# Revit family: Casement_36_I_Top_Hung_Standard
name_source: partatom
category: Windows
revit_build: Autodesk Revit 2014 (Build: 20130308_1515(x64)
units: mm (PartAtom-declared; Revit-internal decimal feet)

## types (24) — shared parameters
Aluminium Thickness = 1 mm  [stored 0.00328084 ft]
Bead SG Gap = 13 mm  [stored 0.0426509 ft]
Bottom Hung = No
Casement Dimension = 36 mm  [stored 0.11811 ft]
Custom Sash Bottom Height = 554 mm  [stored 1.81759 ft]
Custom Sash Top Height = 554 mm  [stored 1.81759 ft]
DG Extrusion Start = 8 mm  [stored 0.0262467 ft]
DG Gasket Finish = Double Glazing Gasket Material
Default Sill Height = 800 mm  [stored 2.62467 ft]
Depth Bead = 22 mm  [stored 0.0721785 ft]
Description = Window 36mm, Type I top hung
Frame Center Offset = 18 mm  [stored 0.0590551 ft]
Height Panel 1 = 540 mm  [stored 1.77165 ft]
Height Panel 2 = 540 mm  [stored 1.77165 ft]
Height Sash Bottom = 524 mm  [stored 1.71916 ft]
Height Sash Bottom Opening = 554 mm  [stored 1.81759 ft]
Height Sash Top = 524 mm  [stored 1.71916 ft]
Height Sash Top Opening = 554 mm  [stored 1.81759 ft]
Limit Fixed Pane Height Max = 1800 mm
Limit Fixed Pane Height Min = 200 mm  [stored 0.656168 ft]
Limit Fixed Pane Width Max = 1500 mm
Limit Fixed Pane Width Min = 200 mm  [stored 0.656168 ft]
Limit Sash Bottom Height Min = 300 mm  [stored 0.984252 ft]
Limit Sash Top Height Max = 900 mm  [stored 2.95276 ft]
Limit Sash Top Height Min = 300 mm  [stored 0.984252 ft]
Limit Sash Width Max = 1200 mm
Limit Sash Width Min = 300 mm  [stored 0.984252 ft]
Limit Window Height Max = 1860 mm
Limit Window Height Min = 1400 mm
Manufacturer = Crealco
Max System DG One Piece Thickness = 6 mm  [stored 0.019685 ft]
Max System DG Unit Thickness = 25 mm  [stored 0.082021 ft]
Model = Casement 36
Offset Bead SG Center Reversed = 18 mm  [stored 0.0590551 ft]
Offset Panel 3 Bead Top = 1170 mm
Offset Sash 1 Top = 23 mm  [stored 0.0754593 ft]
Offset Sash 2 Top = 593 mm  [stored 1.94554 ft]
Offset Sash Left = 23 mm  [stored 0.0754593 ft]
Offset Transom 1 Top = 570 mm  [stored 1.87008 ft]
Offset Transom 2 Top = 1140 mm
Offset Window Exterior = 18 mm  [stored 0.0590551 ft]
SG Gasket Thickness = 6 mm  [stored 0.019685 ft]
Sash Center Offset = 15 mm  [stored 0.0492126 ft]
Sash Overlap = 7 mm  [stored 0.0229659 ft]
Sash Spacing Inner = 8 mm  [stored 0.0262467 ft]
Top Hung = Yes
URL = http://www.crealco.co.za
Wall Closure = By host
Width Bead = 15 mm  [stored 0.0492126 ft]
Width Profile = 30 mm  [stored 0.0984252 ft]
zero-valued in all types: Window Exterior Offset

## per-type parameters (varying)
- 36-1215DT-1000Pa: Area Pane Left Bottom=0.15 m²; Area Pane Left Middle=0.23 m²; Area Pane Left Top=0.23 m²; Area Pane Right=0.78 m²; Clearvue Insulated LowE SHGC Value=0.695; Clearvue Insulated LowE U Value=5.21; Clearvue Insulated SHGC Value=0.762; Clearvue Insulated U Value=5.93; Clearvue SHGC Value=0.866; Clearvue U Value=8.94; Custom Sash Width=554 mm  [stored 1.81759 ft]; Custom Windload=1000 mm; Custom Window Height=1490 mm; Custom Window Width=1190 mm; DG Thickness Calc=4 mm  [stored 0.0131234 ft]; Depth Mullion=54 mm  [stored 0.177165 ft]; Energy Advantage SHGC Value=0.776; Energy Advantage U Value=6.89; Height=1490 mm; Height Panel 3=290 mm  [stored 0.951444 ft]; Height Panel 4=1430 mm; Intruderprufe Insulated LowE SHGC Value=0.641; Intruderprufe Insulated LowE U Value=5.09; Intruderprufe Insulated SHGC Value=0.699; Intruderprufe Insulated U Value=5.78; Intruderprufe LowE SHGC Value=0.727; Intruderprufe LowE U Value=6.73; Intruderprufe SHGC Value=0.825; Intruderprufe U Value=8.74; Length Mullion=1490 mm; Length Transom=540 mm  [stored 1.77165 ft]; Limit Sash Bottom Height Max=644 mm  [stored 2.11286 ft]; Limit Sash Bottom Height Max Based On Top Sash=644 mm  [stored 2.11286 ft]; Limit Sash Bottom Height Max Calc=644 mm  [stored 2.11286 ft]; Limit Window Width Max=2130 mm; Limit Window Width Min=830 mm  [stored 2.7231 ft]; Max Pane Area=0.78 m²; Mullion Depth Windload Based=54 mm  [stored 0.177165 ft]; Offset Mullion Left=570 mm  [stored 1.87008 ft]; Offset Panel 4 Left=600 mm  [stored 1.9685 ft]; Width=1190 mm; Width Panel 1=540 mm  [stored 1.77165 ft]; Width Panel 2=540 mm  [stored 1.77165 ft]; Width Panel 3=540 mm  [stored 1.77165 ft]; Width Panel 4=560 mm  [stored 1.83727 ft]; Width Sash 1=524 mm  [stored 1.71916 ft]; Width Sash 2=524 mm  [stored 1.71916 ft]; Width Sash Opening=554 mm  [stored 1.81759 ft]; Windload Design=1000 mm
- 36-1515DT-1000Pa: Area Pane Left Bottom=0.15 m²; Area Pane Left Middle=0.23 m²; Area Pane Left Top=0.23 m²; Area Pane Right=1.21 m²; Clearvue Insulated LowE SHGC Value=0.809; Clearvue Insulated LowE U Value=5.28; Clearvue Insulated SHGC Value=0.888; Clearvue Insulated U Value=6.15; Clearvue SHGC Value=1.009; Clearvue U Value=9.7; Custom Sash Width=554 mm  [stored 1.81759 ft]; Custom Windload=1000 mm; Custom Window Height=1490 mm; Custom Window Width=1490 mm; DG Thickness Calc=4 mm  [stored 0.0131234 ft]; Depth Mullion=54 mm  [stored 0.177165 ft]; Energy Advantage SHGC Value=0.903; Energy Advantage U Value=7.27; Height=1490 mm; Height Panel 3=290 mm  [stored 0.951444 ft]; Height Panel 4=1430 mm; Intruderprufe Insulated LowE SHGC Value=0.745; Intruderprufe Insulated LowE U Value=5.16; Intruderprufe Insulated SHGC Value=0.815; Intruderprufe Insulated U Value=6; Intruderprufe LowE SHGC Value=0.845; Intruderprufe LowE U Value=7.1; Intruderprufe SHGC Value=0.96; Intruderprufe U Value=9.48; Length Mullion=1490 mm; Length Transom=540 mm  [stored 1.77165 ft]; Limit Sash Bottom Height Max=644 mm  [stored 2.11286 ft]; Limit Sash Bottom Height Max Based On Top Sash=644 mm  [stored 2.11286 ft]; Limit Sash Bottom Height Max Calc=644 mm  [stored 2.11286 ft]; Limit Window Width Max=2130 mm; Limit Window Width Min=830 mm  [stored 2.7231 ft]; Max Pane Area=1.21 m²; Mullion Depth Windload Based=54 mm  [stored 0.177165 ft]; Offset Mullion Left=570 mm  [stored 1.87008 ft]; Offset Panel 4 Left=600 mm  [stored 1.9685 ft]; Width=1490 mm; Width Panel 1=540 mm  [stored 1.77165 ft]; Width Panel 2=540 mm  [stored 1.77165 ft]; Width Panel 3=540 mm  [stored 1.77165 ft]; Width Panel 4=860 mm  [stored 2.82152 ft]; Width Sash 1=524 mm  [stored 1.71916 ft]; Width Sash 2=524 mm  [stored 1.71916 ft]; Width Sash Opening=554 mm  [stored 1.81759 ft]; Windload Design=1000 mm
- 36-1815DT-1000Pa: Area Pane Left Bottom=0.25 m²; Area Pane Left Middle=0.4 m²; Area Pane Left Top=0.4 m²; Area Pane Right=1.14 m²; Clearvue Insulated LowE SHGC Value=0.744; Clearvue Insulated LowE U Value=4.78; Clearvue Insulated SHGC Value=0.816; Clearvue Insulated U Value=5.58; Clearvue SHGC Value=0.927; Clearvue U Value=8.84; Custom Sash Width=900 mm  [stored 2.95276 ft]; Custom Windload=1000 mm; Custom Window Height=1490 mm; Custom Window Width=1790 mm; DG Thickness Calc=4 mm  [stored 0.0131234 ft]; Depth Mullion=54 mm  [stored 0.177165 ft]; Energy Advantage SHGC Value=0.83; Energy Advantage U Value=6.6; Height=1490 mm; Height Panel 3=290 mm  [stored 0.951444 ft]; Height Panel 4=1430 mm; Intruderprufe Insulated LowE SHGC Value=0.684; Intruderprufe Insulated LowE U Value=4.67; Intruderprufe Insulated SHGC Value=0.749; Intruderprufe Insulated U Value=5.44; Intruderprufe LowE SHGC Value=0.776; Intruderprufe LowE U Value=6.45; Intruderprufe SHGC Value=0.882; Intruderprufe U Value=8.64; Length Mullion=1490 mm; Length Transom=886 mm  [stored 2.90682 ft]; Limit Sash Bottom Height Max=644 mm  [stored 2.11286 ft]; Limit Sash Bottom Height Max Based On Top Sash=644 mm  [stored 2.11286 ft]; Limit Sash Bottom Height Max Calc=644 mm  [stored 2.11286 ft]; Limit Window Width Max=2476 mm; Limit Window Width Min=1176 mm; Max Pane Area=1.14 m²; Mullion Depth Windload Based=54 mm  [stored 0.177165 ft]; Offset Mullion Left=916 mm  [stored 3.00525 ft]; Offset Panel 4 Left=946 mm; Width=1790 mm; Width Panel 1=886 mm  [stored 2.90682 ft]; Width Panel 2=886 mm  [stored 2.90682 ft]; Width Panel 3=886 mm  [stored 2.90682 ft]; Width Panel 4=814 mm; Width Sash 1=870 mm  [stored 2.85433 ft]; Width Sash 2=870 mm  [stored 2.85433 ft]; Width Sash Opening=900 mm  [stored 2.95276 ft]; Windload Design=1000 mm
- 36-2415DT-1000Pa: Area Pane Left Bottom=0.51 m²; Area Pane Left Middle=0.4 m²; Area Pane Left Top=0.4 m²; Area Pane Right=2.41 m²; Clearvue Insulated LowE SHGC Value=0.881; Clearvue Insulated LowE U Value=4.94; Clearvue Insulated SHGC Value=0.968; Clearvue Insulated U Value=5.91; Clearvue SHGC Value=0; Clearvue U Value=7.9; Custom Sash Width=900 mm  [stored 2.95276 ft]; Custom Windload=1000 mm; Custom Window Height=1790 mm; Custom Window Width=2390 mm; DG Thickness Calc=5 mm  [stored 0.0164042 ft]; Depth Mullion=70 mm  [stored 0.229659 ft]; Energy Advantage SHGC Value=0; Energy Advantage U Value=7.9; Height=1790 mm; Height Panel 3=590 mm; Height Panel 4=1730 mm; Intruderprufe Insulated LowE SHGC Value=0.81; Intruderprufe Insulated LowE U Value=4.83; Intruderprufe Insulated SHGC Value=0.889; Intruderprufe Insulated U Value=5.76; Intruderprufe LowE SHGC Value=0.919; Intruderprufe LowE U Value=6.97; Intruderprufe SHGC Value=1.046; Intruderprufe U Value=9.6; Length Mullion=1790 mm; Length Transom=886 mm  [stored 2.90682 ft]; Limit Sash Bottom Height Max=900 mm  [stored 2.95276 ft]; Limit Sash Bottom Height Max Based On Top Sash=944 mm; Limit Sash Bottom Height Max Calc=900 mm  [stored 2.95276 ft]; Limit Window Width Max=2476 mm; Limit Window Width Min=1176 mm; Max Pane Area=2.41 m²; Mullion Depth Windload Based=70 mm  [stored 0.229659 ft]; Offset Mullion Left=916 mm  [stored 3.00525 ft]; Offset Panel 4 Left=946 mm; Width=2390 mm; Width Panel 1=886 mm  [stored 2.90682 ft]; Width Panel 2=886 mm  [stored 2.90682 ft]; Width Panel 3=886 mm  [stored 2.90682 ft]; Width Panel 4=1414 mm; Width Sash 1=870 mm  [stored 2.85433 ft]; Width Sash 2=870 mm  [stored 2.85433 ft]; Width Sash Opening=900 mm  [stored 2.95276 ft]; Windload Design=1000 mm
- 36-1818DT-1000Pa: Area Pane Left Bottom=0.51 m²; Area Pane Left Middle=0.4 m²; Area Pane Left Top=0.4 m²; Area Pane Right=1.38 m²; Clearvue Insulated LowE SHGC Value=0.803; Clearvue Insulated LowE U Value=4.83; Clearvue Insulated SHGC Value=0.822; Clearvue Insulated U Value=5.7; Clearvue SHGC Value=0; Clearvue U Value=7.9; Custom Sash Width=900 mm  [stored 2.95276 ft]; Custom Windload=1000 mm; Custom Window Height=1790 mm; Custom Window Width=1790 mm; DG Thickness Calc=4 mm  [stored 0.0131234 ft]; Depth Mullion=70 mm  [stored 0.229659 ft]; Energy Advantage SHGC Value=0; Energy Advantage U Value=7.9; Height=1790 mm; Height Panel 3=590 mm; Height Panel 4=1730 mm; Intruderprufe Insulated LowE SHGC Value=0.739; Intruderprufe Insulated LowE U Value=4.72; Intruderprufe Insulated SHGC Value=0.81; Intruderprufe Insulated U Value=5.56; Intruderprufe LowE SHGC Value=0.839; Intruderprufe LowE U Value=6.66; Intruderprufe SHGC Value=0.953; Intruderprufe U Value=9.04; Length Mullion=1790 mm; Length Transom=886 mm  [stored 2.90682 ft]; Limit Sash Bottom Height Max=900 mm  [stored 2.95276 ft]; Limit Sash Bottom Height Max Based On Top Sash=944 mm; Limit Sash Bottom Height Max Calc=900 mm  [stored 2.95276 ft]; Limit Window Width Max=2476 mm; Limit Window Width Min=1176 mm; Max Pane Area=1.38 m²; Mullion Depth Windload Based=70 mm  [stored 0.229659 ft]; Offset Mullion Left=916 mm  [stored 3.00525 ft]; Offset Panel 4 Left=946 mm; Width=1790 mm; Width Panel 1=886 mm  [stored 2.90682 ft]; Width Panel 2=886 mm  [stored 2.90682 ft]; Width Panel 3=886 mm  [stored 2.90682 ft]; Width Panel 4=814 mm; Width Sash 1=870 mm  [stored 2.85433 ft]; Width Sash 2=870 mm  [stored 2.85433 ft]; Width Sash Opening=900 mm  [stored 2.95276 ft]; Windload Design=1000 mm
- 36-2418DT-1000Pa: Area Pane Left Bottom=0.51 m²; Area Pane Left Middle=0.4 m²; Area Pane Left Top=0.4 m²; Area Pane Right=2.41 m²; Clearvue Insulated LowE SHGC Value=0; Clearvue Insulated LowE U Value=7.9; Clearvue Insulated SHGC Value=0; Clearvue Insulated U Value=7.9; Clearvue SHGC Value=0; Clearvue U Value=7.9; Custom Sash Width=900 mm  [stored 2.95276 ft]; Custom Windload=1000 mm; Custom Window Height=1790 mm; Custom Window Width=2390 mm; DG Thickness Calc=5 mm  [stored 0.0164042 ft]; Depth Mullion=70 mm  [stored 0.229659 ft]; Energy Advantage SHGC Value=0; Energy Advantage U Value=7.9; Height=1790 mm; Height Panel 3=590 mm; Height Panel 4=1730 mm; Intruderprufe Insulated LowE SHGC Value=0.889; Intruderprufe Insulated LowE U Value=4.99; Intruderprufe Insulated SHGC Value=0.977; Intruderprufe Insulated U Value=6.03; Intruderprufe LowE SHGC Value=7.008; Intruderprufe LowE U Value=7.35; Intruderprufe SHGC Value=1.148; Intruderprufe U Value=10.26; Length Mullion=1790 mm; Length Transom=886 mm  [stored 2.90682 ft]; Limit Sash Bottom Height Max=900 mm  [stored 2.95276 ft]; Limit Sash Bottom Height Max Based On Top Sash=944 mm; Limit Sash Bottom Height Max Calc=900 mm  [stored 2.95276 ft]; Limit Window Width Max=2476 mm; Limit Window Width Min=1176 mm; Max Pane Area=2.41 m²; Mullion Depth Windload Based=70 mm  [stored 0.229659 ft]; Offset Mullion Left=916 mm  [stored 3.00525 ft]; Offset Panel 4 Left=946 mm; Width=2390 mm; Width Panel 1=886 mm  [stored 2.90682 ft]; Width Panel 2=886 mm  [stored 2.90682 ft]; Width Panel 3=886 mm  [stored 2.90682 ft]; Width Panel 4=1414 mm; Width Sash 1=870 mm  [stored 2.85433 ft]; Width Sash 2=870 mm  [stored 2.85433 ft]; Width Sash Opening=900 mm  [stored 2.95276 ft]; Windload Design=1000 mm
- 36-1218DT-1000Pa: Area Pane Left Bottom=0.31 m²; Area Pane Left Middle=0.23 m²; Area Pane Left Top=0.23 m²; Area Pane Right=0.95 m²; Clearvue Insulated LowE SHGC Value=0.752; Clearvue Insulated LowE U Value=5.29; Clearvue Insulated SHGC Value=0.825; Clearvue Insulated U Value=6.08; Clearvue SHGC Value=0.937; Clearvue U Value=9.35; Custom Sash Width=554 mm  [stored 1.81759 ft]; Custom Windload=1000 mm; Custom Window Height=1790 mm; Custom Window Width=1190 mm; DG Thickness Calc=4 mm  [stored 0.0131234 ft]; Depth Mullion=54 mm  [stored 0.177165 ft]; Energy Advantage SHGC Value=0.84; Energy Advantage U Value=7.11; Height=1790 mm; Height Panel 3=590 mm; Height Panel 4=1730 mm; Intruderprufe Insulated LowE SHGC Value=0.694; Intruderprufe Insulated LowE U Value=5.15; Intruderprufe Insulated SHGC Value=0.757; Intruderprufe Insulated U Value=5.93; Intruderprufe LowE SHGC Value=0.787; Intruderprufe LowE U Value=6.95; Intruderprufe SHGC Value=0.893; Intruderprufe U Value=9.14; Length Mullion=1790 mm; Length Transom=540 mm  [stored 1.77165 ft]; Limit Sash Bottom Height Max=900 mm  [stored 2.95276 ft]; Limit Sash Bottom Height Max Based On Top Sash=944 mm; Limit Sash Bottom Height Max Calc=900 mm  [stored 2.95276 ft]; Limit Window Width Max=2130 mm; Limit Window Width Min=830 mm  [stored 2.7231 ft]; Max Pane Area=0.95 m²; Mullion Depth Windload Based=54 mm  [stored 0.177165 ft]; Offset Mullion Left=570 mm  [stored 1.87008 ft]; Offset Panel 4 Left=600 mm  [stored 1.9685 ft]; Width=1190 mm; Width Panel 1=540 mm  [stored 1.77165 ft]; Width Panel 2=540 mm  [stored 1.77165 ft]; Width Panel 3=540 mm  [stored 1.77165 ft]; Width Panel 4=560 mm  [stored 1.83727 ft]; Width Sash 1=524 mm  [stored 1.71916 ft]; Width Sash 2=524 mm  [stored 1.71916 ft]; Width Sash Opening=554 mm  [stored 1.81759 ft]; Windload Design=1000 mm
- 36-1518DT-1000Pa: Area Pane Left Bottom=0.31 m²; Area Pane Left Middle=0.23 m²; Area Pane Left Top=0.23 m²; Area Pane Right=1.46 m²; Clearvue Insulated LowE SHGC Value=0.885; Clearvue Insulated LowE U Value=5.45; Clearvue Insulated SHGC Value=0.972; Clearvue Insulated U Value=6.41; Clearvue SHGC Value=0; Clearvue U Value=7.9; Custom Sash Width=554 mm  [stored 1.81759 ft]; Custom Windload=1000 mm; Custom Window Height=1790 mm; Custom Window Width=1490 mm; DG Thickness Calc=4 mm  [stored 0.0131234 ft]; Depth Mullion=70 mm  [stored 0.229659 ft]; Energy Advantage SHGC Value=0; Energy Advantage U Value=7.9; Height=1790 mm; Height Panel 3=590 mm; Height Panel 4=1730 mm; Intruderprufe Insulated LowE SHGC Value=0.816; Intruderprufe Insulated LowE U Value=5.3; Intruderprufe Insulated SHGC Value=0.893; Intruderprufe Insulated U Value=6.25; Intruderprufe LowE SHGC Value=0.925; Intruderprufe LowE U Value=7.46; Intruderprufe SHGC Value=1.051; Intruderprufe U Value=10.08; Length Mullion=1790 mm; Length Transom=540 mm  [stored 1.77165 ft]; Limit Sash Bottom Height Max=900 mm  [stored 2.95276 ft]; Limit Sash Bottom Height Max Based On Top Sash=944 mm; Limit Sash Bottom Height Max Calc=900 mm  [stored 2.95276 ft]; Limit Window Width Max=2130 mm; Limit Window Width Min=830 mm  [stored 2.7231 ft]; Max Pane Area=1.46 m²; Mullion Depth Windload Based=70 mm  [stored 0.229659 ft]; Offset Mullion Left=570 mm  [stored 1.87008 ft]; Offset Panel 4 Left=600 mm  [stored 1.9685 ft]; Width=1490 mm; Width Panel 1=540 mm  [stored 1.77165 ft]; Width Panel 2=540 mm  [stored 1.77165 ft]; Width Panel 3=540 mm  [stored 1.77165 ft]; Width Panel 4=860 mm  [stored 2.82152 ft]; Width Sash 1=524 mm  [stored 1.71916 ft]; Width Sash 2=524 mm  [stored 1.71916 ft]; Width Sash Opening=554 mm  [stored 1.81759 ft]; Windload Design=1000 mm
- 36-1215DT-1500Pa: Area Pane Left Bottom=0.15 m²; Area Pane Left Middle=0.23 m²; Area Pane Left Top=0.23 m²; Area Pane Right=0.78 m²; Clearvue Insulated LowE SHGC Value=0.695; Clearvue Insulated LowE U Value=5.21; Clearvue Insulated SHGC Value=0.762; Clearvue Insulated U Value=5.93; Clearvue SHGC Value=0.866; Clearvue U Value=8.94; Custom Sash Width=554 mm  [stored 1.81759 ft]; Custom Windload=1500 mm; Custom Window Height=1490 mm; Custom Window Width=1190 mm; DG Thickness Calc=4 mm  [stored 0.0131234 ft]; Depth Mullion=54 mm  [stored 0.177165 ft]; Energy Advantage SHGC Value=0.776; Energy Advantage U Value=6.89; Height=1490 mm; Height Panel 3=290 mm  [stored 0.951444 ft]; Height Panel 4=1430 mm; Intruderprufe Insulated LowE SHGC Value=0.641; Intruderprufe Insulated LowE U Value=5.09; Intruderprufe Insulated SHGC Value=0.699; Intruderprufe Insulated U Value=5.78; Intruderprufe LowE SHGC Value=0.727; Intruderprufe LowE U Value=6.73; Intruderprufe SHGC Value=0.825; Intruderprufe U Value=8.74; Length Mullion=1490 mm; Length Transom=540 mm  [stored 1.77165 ft]; Limit Sash Bottom Height Max=644 mm  [stored 2.11286 ft]; Limit Sash Bottom Height Max Based On Top Sash=644 mm  [stored 2.11286 ft]; Limit Sash Bottom Height Max Calc=644 mm  [stored 2.11286 ft]; Limit Window Width Max=2130 mm; Limit Window Width Min=830 mm  [stored 2.7231 ft]; Max Pane Area=0.78 m²; Mullion Depth Windload Based=54 mm  [stored 0.177165 ft]; Offset Mullion Left=570 mm  [stored 1.87008 ft]; Offset Panel 4 Left=600 mm  [stored 1.9685 ft]; Width=1190 mm; Width Panel 1=540 mm  [stored 1.77165 ft]; Width Panel 2=540 mm  [stored 1.77165 ft]; Width Panel 3=540 mm  [stored 1.77165 ft]; Width Panel 4=560 mm  [stored 1.83727 ft]; Width Sash 1=524 mm  [stored 1.71916 ft]; Width Sash 2=524 mm  [stored 1.71916 ft]; Width Sash Opening=554 mm  [stored 1.81759 ft]; Windload Design=1500 mm
- 36-1215DT-2000Pa: Area Pane Left Bottom=0.15 m²; Area Pane Left Middle=0.23 m²; Area Pane Left Top=0.23 m²; Area Pane Right=0.78 m²; Clearvue Insulated LowE SHGC Value=0.695; Clearvue Insulated LowE U Value=5.21; Clearvue Insulated SHGC Value=0.762; Clearvue Insulated U Value=5.93; Clearvue SHGC Value=0.866; Clearvue U Value=8.94; Custom Sash Width=554 mm  [stored 1.81759 ft]; Custom Windload=2000 mm; Custom Window Height=1490 mm; Custom Window Width=1190 mm; DG Thickness Calc=4 mm  [stored 0.0131234 ft]; Depth Mullion=54 mm  [stored 0.177165 ft]; Energy Advantage SHGC Value=0.776; Energy Advantage U Value=6.89; Height=1490 mm; Height Panel 3=290 mm  [stored 0.951444 ft]; Height Panel 4=1430 mm; Intruderprufe Insulated LowE SHGC Value=0.641; Intruderprufe Insulated LowE U Value=5.09; Intruderprufe Insulated SHGC Value=0.699; Intruderprufe Insulated U Value=5.78; Intruderprufe LowE SHGC Value=0.727; Intruderprufe LowE U Value=6.73; Intruderprufe SHGC Value=0.825; Intruderprufe U Value=8.74; Length Mullion=1490 mm; Length Transom=540 mm  [stored 1.77165 ft]; Limit Sash Bottom Height Max=644 mm  [stored 2.11286 ft]; Limit Sash Bottom Height Max Based On Top Sash=644 mm  [stored 2.11286 ft]; Limit Sash Bottom Height Max Calc=644 mm  [stored 2.11286 ft]; Limit Window Width Max=2130 mm; Limit Window Width Min=830 mm  [stored 2.7231 ft]; Max Pane Area=0.78 m²; Mullion Depth Windload Based=54 mm  [stored 0.177165 ft]; Offset Mullion Left=570 mm  [stored 1.87008 ft]; Offset Panel 4 Left=600 mm  [stored 1.9685 ft]; Width=1190 mm; Width Panel 1=540 mm  [stored 1.77165 ft]; Width Panel 2=540 mm  [stored 1.77165 ft]; Width Panel 3=540 mm  [stored 1.77165 ft]; Width Panel 4=560 mm  [stored 1.83727 ft]; Width Sash 1=524 mm  [stored 1.71916 ft]; Width Sash 2=524 mm  [stored 1.71916 ft]; Width Sash Opening=554 mm  [stored 1.81759 ft]; Windload Design=2000 mm
- 36-1515DT-1500Pa: Area Pane Left Bottom=0.15 m²; Area Pane Left Middle=0.23 m²; Area Pane Left Top=0.23 m²; Area Pane Right=1.21 m²; Clearvue Insulated LowE SHGC Value=0.809; Clearvue Insulated LowE U Value=5.28; Clearvue Insulated SHGC Value=0.888; Clearvue Insulated U Value=6.15; Clearvue SHGC Value=1.009; Clearvue U Value=9.7; Custom Sash Width=554 mm  [stored 1.81759 ft]; Custom Windload=1500 mm; Custom Window Height=1490 mm; Custom Window Width=1490 mm; DG Thickness Calc=4 mm  [stored 0.0131234 ft]; Depth Mullion=54 mm  [stored 0.177165 ft]; Energy Advantage SHGC Value=0.903; Energy Advantage U Value=7.27; Height=1490 mm; Height Panel 3=290 mm  [stored 0.951444 ft]; Height Panel 4=1430 mm; Intruderprufe Insulated LowE SHGC Value=0.745; Intruderprufe Insulated LowE U Value=5.16; Intruderprufe Insulated SHGC Value=0.815; Intruderprufe Insulated U Value=6; Intruderprufe LowE SHGC Value=0.845; Intruderprufe LowE U Value=7.1; Intruderprufe SHGC Value=0.96; Intruderprufe U Value=9.48; Length Mullion=1490 mm; Length Transom=540 mm  [stored 1.77165 ft]; Limit Sash Bottom Height Max=644 mm  [stored 2.11286 ft]; Limit Sash Bottom Height Max Based On Top Sash=644 mm  [stored 2.11286 ft]; Limit Sash Bottom Height Max Calc=644 mm  [stored 2.11286 ft]; Limit Window Width Max=2130 mm; Limit Window Width Min=830 mm  [stored 2.7231 ft]; Max Pane Area=1.21 m²; Mullion Depth Windload Based=54 mm  [stored 0.177165 ft]; Offset Mullion Left=570 mm  [stored 1.87008 ft]; Offset Panel 4 Left=600 mm  [stored 1.9685 ft]; Width=1490 mm; Width Panel 1=540 mm  [stored 1.77165 ft]; Width Panel 2=540 mm  [stored 1.77165 ft]; Width Panel 3=540 mm  [stored 1.77165 ft]; Width Panel 4=860 mm  [stored 2.82152 ft]; Width Sash 1=524 mm  [stored 1.71916 ft]; Width Sash 2=524 mm  [stored 1.71916 ft]; Width Sash Opening=554 mm  [stored 1.81759 ft]; Windload Design=1500 mm
- 36-1515DT-2000Pa: Area Pane Left Bottom=0.15 m²; Area Pane Left Middle=0.23 m²; Area Pane Left Top=0.23 m²; Area Pane Right=1.21 m²; Clearvue Insulated LowE SHGC Value=0.809; Clearvue Insulated LowE U Value=5.28; Clearvue Insulated SHGC Value=0.888; Clearvue Insulated U Value=6.15; Clearvue SHGC Value=1.009; Clearvue U Value=9.7; Custom Sash Width=554 mm  [stored 1.81759 ft]; Custom Windload=2000 mm; Custom Window Height=1490 mm; Custom Window Width=1490 mm; DG Thickness Calc=4 mm  [stored 0.0131234 ft]; Depth Mullion=70 mm  [stored 0.229659 ft]; Energy Advantage SHGC Value=0.903; Energy Advantage U Value=7.27; Height=1490 mm; Height Panel 3=290 mm  [stored 0.951444 ft]; Height Panel 4=1430 mm; Intruderprufe Insulated LowE SHGC Value=0.745; Intruderprufe Insulated LowE U Value=5.16; Intruderprufe Insulated SHGC Value=0.815; Intruderprufe Insulated U Value=6; Intruderprufe LowE SHGC Value=0.845; Intruderprufe LowE U Value=7.1; Intruderprufe SHGC Value=0.96; Intruderprufe U Value=9.48; Length Mullion=1490 mm; Length Transom=540 mm  [stored 1.77165 ft]; Limit Sash Bottom Height Max=644 mm  [stored 2.11286 ft]; Limit Sash Bottom Height Max Based On Top Sash=644 mm  [stored 2.11286 ft]; Limit Sash Bottom Height Max Calc=644 mm  [stored 2.11286 ft]; Limit Window Width Max=2130 mm; Limit Window Width Min=830 mm  [stored 2.7231 ft]; Max Pane Area=1.21 m²; Mullion Depth Windload Based=70 mm  [stored 0.229659 ft]; Offset Mullion Left=570 mm  [stored 1.87008 ft]; Offset Panel 4 Left=600 mm  [stored 1.9685 ft]; Width=1490 mm; Width Panel 1=540 mm  [stored 1.77165 ft]; Width Panel 2=540 mm  [stored 1.77165 ft]; Width Panel 3=540 mm  [stored 1.77165 ft]; Width Panel 4=860 mm  [stored 2.82152 ft]; Width Sash 1=524 mm  [stored 1.71916 ft]; Width Sash 2=524 mm  [stored 1.71916 ft]; Width Sash Opening=554 mm  [stored 1.81759 ft]; Windload Design=2000 mm
- 36-1815DT-1500Pa: Area Pane Left Bottom=0.25 m²; Area Pane Left Middle=0.4 m²; Area Pane Left Top=0.4 m²; Area Pane Right=1.14 m²; Clearvue Insulated LowE SHGC Value=0.744; Clearvue Insulated LowE U Value=4.78; Clearvue Insulated SHGC Value=0.816; Clearvue Insulated U Value=5.58; Clearvue SHGC Value=0.927; Clearvue U Value=8.84; Custom Sash Width=900 mm  [stored 2.95276 ft]; Custom Windload=1500 mm; Custom Window Height=1490 mm; Custom Window Width=1790 mm; DG Thickness Calc=4 mm  [stored 0.0131234 ft]; Depth Mullion=70 mm  [stored 0.229659 ft]; Energy Advantage SHGC Value=0.83; Energy Advantage U Value=6.6; Height=1490 mm; Height Panel 3=290 mm  [stored 0.951444 ft]; Height Panel 4=1430 mm; Intruderprufe Insulated LowE SHGC Value=0.684; Intruderprufe Insulated LowE U Value=4.67; Intruderprufe Insulated SHGC Value=0.749; Intruderprufe Insulated U Value=5.44; Intruderprufe LowE SHGC Value=0.776; Intruderprufe LowE U Value=6.45; Intruderprufe SHGC Value=0.882; Intruderprufe U Value=8.64; Length Mullion=1490 mm; Length Transom=886 mm  [stored 2.90682 ft]; Limit Sash Bottom Height Max=644 mm  [stored 2.11286 ft]; Limit Sash Bottom Height Max Based On Top Sash=644 mm  [stored 2.11286 ft]; Limit Sash Bottom Height Max Calc=644 mm  [stored 2.11286 ft]; Limit Window Width Max=2476 mm; Limit Window Width Min=1176 mm; Max Pane Area=1.14 m²; Mullion Depth Windload Based=70 mm  [stored 0.229659 ft]; Offset Mullion Left=916 mm  [stored 3.00525 ft]; Offset Panel 4 Left=946 mm; Width=1790 mm; Width Panel 1=886 mm  [stored 2.90682 ft]; Width Panel 2=886 mm  [stored 2.90682 ft]; Width Panel 3=886 mm  [stored 2.90682 ft]; Width Panel 4=814 mm; Width Sash 1=870 mm  [stored 2.85433 ft]; Width Sash 2=870 mm  [stored 2.85433 ft]; Width Sash Opening=900 mm  [stored 2.95276 ft]; Windload Design=1500 mm
- 36-1815DT-2000Pa: Area Pane Left Bottom=0.25 m²; Area Pane Left Middle=0.4 m²; Area Pane Left Top=0.4 m²; Area Pane Right=1.14 m²; Clearvue Insulated LowE SHGC Value=0.744; Clearvue Insulated LowE U Value=4.78; Clearvue Insulated SHGC Value=0.816; Clearvue Insulated U Value=5.58; Clearvue SHGC Value=0.927; Clearvue U Value=8.84; Custom Sash Width=900 mm  [stored 2.95276 ft]; Custom Windload=2000 mm; Custom Window Height=1490 mm; Custom Window Width=1790 mm; DG Thickness Calc=4 mm  [stored 0.0131234 ft]; Depth Mullion=70 mm  [stored 0.229659 ft]; Energy Advantage SHGC Value=0.83; Energy Advantage U Value=6.6; Height=1490 mm; Height Panel 3=290 mm  [stored 0.951444 ft]; Height Panel 4=1430 mm; Intruderprufe Insulated LowE SHGC Value=0.684; Intruderprufe Insulated LowE U Value=4.67; Intruderprufe Insulated SHGC Value=0.749; Intruderprufe Insulated U Value=5.44; Intruderprufe LowE SHGC Value=0.776; Intruderprufe LowE U Value=6.45; Intruderprufe SHGC Value=0.882; Intruderprufe U Value=8.64; Length Mullion=1490 mm; Length Transom=886 mm  [stored 2.90682 ft]; Limit Sash Bottom Height Max=644 mm  [stored 2.11286 ft]; Limit Sash Bottom Height Max Based On Top Sash=644 mm  [stored 2.11286 ft]; Limit Sash Bottom Height Max Calc=644 mm  [stored 2.11286 ft]; Limit Window Width Max=2476 mm; Limit Window Width Min=1176 mm; Max Pane Area=1.14 m²; Mullion Depth Windload Based=70 mm  [stored 0.229659 ft]; Offset Mullion Left=916 mm  [stored 3.00525 ft]; Offset Panel 4 Left=946 mm; Width=1790 mm; Width Panel 1=886 mm  [stored 2.90682 ft]; Width Panel 2=886 mm  [stored 2.90682 ft]; Width Panel 3=886 mm  [stored 2.90682 ft]; Width Panel 4=814 mm; Width Sash 1=870 mm  [stored 2.85433 ft]; Width Sash 2=870 mm  [stored 2.85433 ft]; Width Sash Opening=900 mm  [stored 2.95276 ft]; Windload Design=2000 mm
- 36-2415DT-1500Pa: Area Pane Left Bottom=0.51 m²; Area Pane Left Middle=0.4 m²; Area Pane Left Top=0.4 m²; Area Pane Right=2.41 m²; Clearvue Insulated LowE SHGC Value=0.881; Clearvue Insulated LowE U Value=4.94; Clearvue Insulated SHGC Value=0.968; Clearvue Insulated U Value=5.91; Clearvue SHGC Value=0; Clearvue U Value=7.9; Custom Sash Width=900 mm  [stored 2.95276 ft]; Custom Windload=1500 mm; Custom Window Height=1790 mm; Custom Window Width=2390 mm; DG Thickness Calc=5 mm  [stored 0.0164042 ft]; Depth Mullion=90 mm  [stored 0.295276 ft]; Energy Advantage SHGC Value=0; Energy Advantage U Value=7.9; Height=1790 mm; Height Panel 3=590 mm; Height Panel 4=1730 mm; Intruderprufe Insulated LowE SHGC Value=0.81; Intruderprufe Insulated LowE U Value=4.83; Intruderprufe Insulated SHGC Value=0.889; Intruderprufe Insulated U Value=5.76; Intruderprufe LowE SHGC Value=0.919; Intruderprufe LowE U Value=6.97; Intruderprufe SHGC Value=1.046; Intruderprufe U Value=9.6; Length Mullion=1790 mm; Length Transom=886 mm  [stored 2.90682 ft]; Limit Sash Bottom Height Max=900 mm  [stored 2.95276 ft]; Limit Sash Bottom Height Max Based On Top Sash=944 mm; Limit Sash Bottom Height Max Calc=900 mm  [stored 2.95276 ft]; Limit Window Width Max=2476 mm; Limit Window Width Min=1176 mm; Max Pane Area=2.41 m²; Mullion Depth Windload Based=90 mm  [stored 0.295276 ft]; Offset Mullion Left=916 mm  [stored 3.00525 ft]; Offset Panel 4 Left=946 mm; Width=2390 mm; Width Panel 1=886 mm  [stored 2.90682 ft]; Width Panel 2=886 mm  [stored 2.90682 ft]; Width Panel 3=886 mm  [stored 2.90682 ft]; Width Panel 4=1414 mm; Width Sash 1=870 mm  [stored 2.85433 ft]; Width Sash 2=870 mm  [stored 2.85433 ft]; Width Sash Opening=900 mm  [stored 2.95276 ft]; Windload Design=1500 mm
- 36-2415DT-2000Pa: Area Pane Left Bottom=0.51 m²; Area Pane Left Middle=0.4 m²; Area Pane Left Top=0.4 m²; Area Pane Right=2.41 m²; Clearvue Insulated LowE SHGC Value=0.881; Clearvue Insulated LowE U Value=4.94; Clearvue Insulated SHGC Value=0.968; Clearvue Insulated U Value=5.91; Clearvue SHGC Value=0; Clearvue U Value=7.9; Custom Sash Width=900 mm  [stored 2.95276 ft]; Custom Windload=2000 mm; Custom Window Height=1790 mm; Custom Window Width=2390 mm; DG Thickness Calc=5 mm  [stored 0.0164042 ft]; Depth Mullion=90 mm  [stored 0.295276 ft]; Energy Advantage SHGC Value=0; Energy Advantage U Value=7.9; Height=1790 mm; Height Panel 3=590 mm; Height Panel 4=1730 mm; Intruderprufe Insulated LowE SHGC Value=0.81; Intruderprufe Insulated LowE U Value=4.83; Intruderprufe Insulated SHGC Value=0.889; Intruderprufe Insulated U Value=5.76; Intruderprufe LowE SHGC Value=0.919; Intruderprufe LowE U Value=6.97; Intruderprufe SHGC Value=1.046; Intruderprufe U Value=9.6; Length Mullion=1790 mm; Length Transom=886 mm  [stored 2.90682 ft]; Limit Sash Bottom Height Max=900 mm  [stored 2.95276 ft]; Limit Sash Bottom Height Max Based On Top Sash=944 mm; Limit Sash Bottom Height Max Calc=900 mm  [stored 2.95276 ft]; Limit Window Width Max=2476 mm; Limit Window Width Min=1176 mm; Max Pane Area=2.41 m²; Mullion Depth Windload Based=90 mm  [stored 0.295276 ft]; Offset Mullion Left=916 mm  [stored 3.00525 ft]; Offset Panel 4 Left=946 mm; Width=2390 mm; Width Panel 1=886 mm  [stored 2.90682 ft]; Width Panel 2=886 mm  [stored 2.90682 ft]; Width Panel 3=886 mm  [stored 2.90682 ft]; Width Panel 4=1414 mm; Width Sash 1=870 mm  [stored 2.85433 ft]; Width Sash 2=870 mm  [stored 2.85433 ft]; Width Sash Opening=900 mm  [stored 2.95276 ft]; Windload Design=2000 mm
- 36-1218DT-1500Pa: Area Pane Left Bottom=0.31 m²; Area Pane Left Middle=0.23 m²; Area Pane Left Top=0.23 m²; Area Pane Right=0.95 m²; Clearvue Insulated LowE SHGC Value=0.752; Clearvue Insulated LowE U Value=5.29; Clearvue Insulated SHGC Value=0.825; Clearvue Insulated U Value=6.08; Clearvue SHGC Value=0.937; Clearvue U Value=9.35; Custom Sash Width=554 mm  [stored 1.81759 ft]; Custom Windload=1500 mm; Custom Window Height=1790 mm; Custom Window Width=1190 mm; DG Thickness Calc=4 mm  [stored 0.0131234 ft]; Depth Mullion=70 mm  [stored 0.229659 ft]; Energy Advantage SHGC Value=0.84; Energy Advantage U Value=7.11; Height=1790 mm; Height Panel 3=590 mm; Height Panel 4=1730 mm; Intruderprufe Insulated LowE SHGC Value=0.694; Intruderprufe Insulated LowE U Value=5.15; Intruderprufe Insulated SHGC Value=0.757; Intruderprufe Insulated U Value=5.93; Intruderprufe LowE SHGC Value=0.787; Intruderprufe LowE U Value=6.95; Intruderprufe SHGC Value=0.893; Intruderprufe U Value=9.14; Length Mullion=1790 mm; Length Transom=540 mm  [stored 1.77165 ft]; Limit Sash Bottom Height Max=900 mm  [stored 2.95276 ft]; Limit Sash Bottom Height Max Based On Top Sash=944 mm; Limit Sash Bottom Height Max Calc=900 mm  [stored 2.95276 ft]; Limit Window Width Max=2130 mm; Limit Window Width Min=830 mm  [stored 2.7231 ft]; Max Pane Area=0.95 m²; Mullion Depth Windload Based=70 mm  [stored 0.229659 ft]; Offset Mullion Left=570 mm  [stored 1.87008 ft]; Offset Panel 4 Left=600 mm  [stored 1.9685 ft]; Width=1190 mm; Width Panel 1=540 mm  [stored 1.77165 ft]; Width Panel 2=540 mm  [stored 1.77165 ft]; Width Panel 3=540 mm  [stored 1.77165 ft]; Width Panel 4=560 mm  [stored 1.83727 ft]; Width Sash 1=524 mm  [stored 1.71916 ft]; Width Sash 2=524 mm  [stored 1.71916 ft]; Width Sash Opening=554 mm  [stored 1.81759 ft]; Windload Design=1500 mm
- 36-1218DT-2000Pa: Area Pane Left Bottom=0.31 m²; Area Pane Left Middle=0.23 m²; Area Pane Left Top=0.23 m²; Area Pane Right=0.95 m²; Clearvue Insulated LowE SHGC Value=0.752; Clearvue Insulated LowE U Value=5.29; Clearvue Insulated SHGC Value=0.825; Clearvue Insulated U Value=6.08; Clearvue SHGC Value=0.937; Clearvue U Value=9.35; Custom Sash Width=554 mm  [stored 1.81759 ft]; Custom Windload=2000 mm; Custom Window Height=1790 mm; Custom Window Width=1190 mm; DG Thickness Calc=4 mm  [stored 0.0131234 ft]; Depth Mullion=70 mm  [stored 0.229659 ft]; Energy Advantage SHGC Value=0.84; Energy Advantage U Value=7.11; Height=1790 mm; Height Panel 3=590 mm; Height Panel 4=1730 mm; Intruderprufe Insulated LowE SHGC Value=0.694; Intruderprufe Insulated LowE U Value=5.15; Intruderprufe Insulated SHGC Value=0.757; Intruderprufe Insulated U Value=5.93; Intruderprufe LowE SHGC Value=0.787; Intruderprufe LowE U Value=6.95; Intruderprufe SHGC Value=0.893; Intruderprufe U Value=9.14; Length Mullion=1790 mm; Length Transom=540 mm  [stored 1.77165 ft]; Limit Sash Bottom Height Max=900 mm  [stored 2.95276 ft]; Limit Sash Bottom Height Max Based On Top Sash=944 mm; Limit Sash Bottom Height Max Calc=900 mm  [stored 2.95276 ft]; Limit Window Width Max=2130 mm; Limit Window Width Min=830 mm  [stored 2.7231 ft]; Max Pane Area=0.95 m²; Mullion Depth Windload Based=70 mm  [stored 0.229659 ft]; Offset Mullion Left=570 mm  [stored 1.87008 ft]; Offset Panel 4 Left=600 mm  [stored 1.9685 ft]; Width=1190 mm; Width Panel 1=540 mm  [stored 1.77165 ft]; Width Panel 2=540 mm  [stored 1.77165 ft]; Width Panel 3=540 mm  [stored 1.77165 ft]; Width Panel 4=560 mm  [stored 1.83727 ft]; Width Sash 1=524 mm  [stored 1.71916 ft]; Width Sash 2=524 mm  [stored 1.71916 ft]; Width Sash Opening=554 mm  [stored 1.81759 ft]; Windload Design=2000 mm
- 36-1518DT-1500Pa: Area Pane Left Bottom=0.31 m²; Area Pane Left Middle=0.23 m²; Area Pane Left Top=0.23 m²; Area Pane Right=1.46 m²; Clearvue Insulated LowE SHGC Value=0.885; Clearvue Insulated LowE U Value=5.45; Clearvue Insulated SHGC Value=0.972; Clearvue Insulated U Value=6.41; Clearvue SHGC Value=0; Clearvue U Value=7.9; Custom Sash Width=554 mm  [stored 1.81759 ft]; Custom Windload=1500 mm; Custom Window Height=1790 mm; Custom Window Width=1490 mm; DG Thickness Calc=4 mm  [stored 0.0131234 ft]; Depth Mullion=70 mm  [stored 0.229659 ft]; Energy Advantage SHGC Value=0; Energy Advantage U Value=7.9; Height=1790 mm; Height Panel 3=590 mm; Height Panel 4=1730 mm; Intruderprufe Insulated LowE SHGC Value=0.816; Intruderprufe Insulated LowE U Value=5.3; Intruderprufe Insulated SHGC Value=0.893; Intruderprufe Insulated U Value=6.25; Intruderprufe LowE SHGC Value=0.925; Intruderprufe LowE U Value=7.46; Intruderprufe SHGC Value=1.051; Intruderprufe U Value=10.08; Length Mullion=1790 mm; Length Transom=540 mm  [stored 1.77165 ft]; Limit Sash Bottom Height Max=900 mm  [stored 2.95276 ft]; Limit Sash Bottom Height Max Based On Top Sash=944 mm; Limit Sash Bottom Height Max Calc=900 mm  [stored 2.95276 ft]; Limit Window Width Max=2130 mm; Limit Window Width Min=830 mm  [stored 2.7231 ft]; Max Pane Area=1.46 m²; Mullion Depth Windload Based=70 mm  [stored 0.229659 ft]; Offset Mullion Left=570 mm  [stored 1.87008 ft]; Offset Panel 4 Left=600 mm  [stored 1.9685 ft]; Width=1490 mm; Width Panel 1=540 mm  [stored 1.77165 ft]; Width Panel 2=540 mm  [stored 1.77165 ft]; Width Panel 3=540 mm  [stored 1.77165 ft]; Width Panel 4=860 mm  [stored 2.82152 ft]; Width Sash 1=524 mm  [stored 1.71916 ft]; Width Sash 2=524 mm  [stored 1.71916 ft]; Width Sash Opening=554 mm  [stored 1.81759 ft]; Windload Design=1500 mm
- 36-1518DT-2000Pa: Area Pane Left Bottom=0.31 m²; Area Pane Left Middle=0.23 m²; Area Pane Left Top=0.23 m²; Area Pane Right=1.46 m²; Clearvue Insulated LowE SHGC Value=0.886; Clearvue Insulated LowE U Value=5.48; Clearvue Insulated SHGC Value=0.973; Clearvue Insulated U Value=6.44; Clearvue SHGC Value=0; Clearvue U Value=7.9; Custom Sash Width=554 mm  [stored 1.81759 ft]; Custom Windload=2000 mm; Custom Window Height=1790 mm; Custom Window Width=1490 mm; DG Thickness Calc=4 mm  [stored 0.0131234 ft]; Depth Mullion=90 mm  [stored 0.295276 ft]; Energy Advantage SHGC Value=0; Energy Advantage U Value=7.9; Height=1790 mm; Height Panel 3=590 mm; Height Panel 4=1730 mm; Intruderprufe Insulated LowE SHGC Value=0.815; Intruderprufe Insulated LowE U Value=5.37; Intruderprufe Insulated SHGC Value=0.894; Intruderprufe Insulated U Value=6.29; Intruderprufe LowE SHGC Value=0.927; Intruderprufe LowE U Value=7.52; Intruderprufe SHGC Value=1.054; Intruderprufe U Value=10.14; Length Mullion=1790 mm; Length Transom=540 mm  [stored 1.77165 ft]; Limit Sash Bottom Height Max=900 mm  [stored 2.95276 ft]; Limit Sash Bottom Height Max Based On Top Sash=944 mm; Limit Sash Bottom Height Max Calc=900 mm  [stored 2.95276 ft]; Limit Window Width Max=2130 mm; Limit Window Width Min=830 mm  [stored 2.7231 ft]; Max Pane Area=1.46 m²; Mullion Depth Windload Based=90 mm  [stored 0.295276 ft]; Offset Mullion Left=570 mm  [stored 1.87008 ft]; Offset Panel 4 Left=600 mm  [stored 1.9685 ft]; Width=1490 mm; Width Panel 1=540 mm  [stored 1.77165 ft]; Width Panel 2=540 mm  [stored 1.77165 ft]; Width Panel 3=540 mm  [stored 1.77165 ft]; Width Panel 4=860 mm  [stored 2.82152 ft]; Width Sash 1=524 mm  [stored 1.71916 ft]; Width Sash 2=524 mm  [stored 1.71916 ft]; Width Sash Opening=554 mm  [stored 1.81759 ft]; Windload Design=2000 mm
- 36-1818DT-1500Pa: Area Pane Left Bottom=0.51 m²; Area Pane Left Middle=0.4 m²; Area Pane Left Top=0.4 m²; Area Pane Right=1.38 m²; Clearvue Insulated LowE SHGC Value=0.803; Clearvue Insulated LowE U Value=4.83; Clearvue Insulated SHGC Value=0.822; Clearvue Insulated U Value=5.7; Clearvue SHGC Value=0; Clearvue U Value=7.9; Custom Sash Width=900 mm  [stored 2.95276 ft]; Custom Windload=1500 mm; Custom Window Height=1790 mm; Custom Window Width=1790 mm; DG Thickness Calc=4 mm  [stored 0.0131234 ft]; Depth Mullion=70 mm  [stored 0.229659 ft]; Energy Advantage SHGC Value=0; Energy Advantage U Value=7.9; Height=1790 mm; Height Panel 3=590 mm; Height Panel 4=1730 mm; Intruderprufe Insulated LowE SHGC Value=0.739; Intruderprufe Insulated LowE U Value=4.72; Intruderprufe Insulated SHGC Value=0.81; Intruderprufe Insulated U Value=5.56; Intruderprufe LowE SHGC Value=0.839; Intruderprufe LowE U Value=6.66; Intruderprufe SHGC Value=0.953; Intruderprufe U Value=9.04; Length Mullion=1790 mm; Length Transom=886 mm  [stored 2.90682 ft]; Limit Sash Bottom Height Max=900 mm  [stored 2.95276 ft]; Limit Sash Bottom Height Max Based On Top Sash=944 mm; Limit Sash Bottom Height Max Calc=900 mm  [stored 2.95276 ft]; Limit Window Width Max=2476 mm; Limit Window Width Min=1176 mm; Max Pane Area=1.38 m²; Mullion Depth Windload Based=70 mm  [stored 0.229659 ft]; Offset Mullion Left=916 mm  [stored 3.00525 ft]; Offset Panel 4 Left=946 mm; Width=1790 mm; Width Panel 1=886 mm  [stored 2.90682 ft]; Width Panel 2=886 mm  [stored 2.90682 ft]; Width Panel 3=886 mm  [stored 2.90682 ft]; Width Panel 4=814 mm; Width Sash 1=870 mm  [stored 2.85433 ft]; Width Sash 2=870 mm  [stored 2.85433 ft]; Width Sash Opening=900 mm  [stored 2.95276 ft]; Windload Design=1500 mm
- 36-1818DT-2000Pa: Area Pane Left Bottom=0.51 m²; Area Pane Left Middle=0.4 m²; Area Pane Left Top=0.4 m²; Area Pane Right=1.38 m²; Clearvue Insulated LowE SHGC Value=0.804; Clearvue Insulated LowE U Value=4.85; Clearvue Insulated SHGC Value=0.882; Clearvue Insulated U Value=5.72; Clearvue SHGC Value=0; Clearvue U Value=7.9; Custom Sash Width=900 mm  [stored 2.95276 ft]; Custom Windload=2000 mm; Custom Window Height=1790 mm; Custom Window Width=1790 mm; DG Thickness Calc=4 mm  [stored 0.0131234 ft]; Depth Mullion=90 mm  [stored 0.295276 ft]; Energy Advantage SHGC Value=0; Energy Advantage U Value=7.9; Height=1790 mm; Height Panel 3=590 mm; Height Panel 4=1730 mm; Intruderprufe Insulated LowE SHGC Value=0.739; Intruderprufe Insulated LowE U Value=4.75; Intruderprufe Insulated SHGC Value=0.811; Intruderprufe Insulated U Value=5.59; Intruderprufe LowE SHGC Value=0.84; Intruderprufe LowE U Value=6.7; Intruderprufe SHGC Value=0.956; Intruderprufe U Value=9.08; Length Mullion=1790 mm; Length Transom=886 mm  [stored 2.90682 ft]; Limit Sash Bottom Height Max=900 mm  [stored 2.95276 ft]; Limit Sash Bottom Height Max Based On Top Sash=944 mm; Limit Sash Bottom Height Max Calc=900 mm  [stored 2.95276 ft]; Limit Window Width Max=2476 mm; Limit Window Width Min=1176 mm; Max Pane Area=1.38 m²; Mullion Depth Windload Based=90 mm  [stored 0.295276 ft]; Offset Mullion Left=916 mm  [stored 3.00525 ft]; Offset Panel 4 Left=946 mm; Width=1790 mm; Width Panel 1=886 mm  [stored 2.90682 ft]; Width Panel 2=886 mm  [stored 2.90682 ft]; Width Panel 3=886 mm  [stored 2.90682 ft]; Width Panel 4=814 mm; Width Sash 1=870 mm  [stored 2.85433 ft]; Width Sash 2=870 mm  [stored 2.85433 ft]; Width Sash Opening=900 mm  [stored 2.95276 ft]; Windload Design=2000 mm
- 36-2418DT-1500Pa: Area Pane Left Bottom=0.51 m²; Area Pane Left Middle=0.4 m²; Area Pane Left Top=0.4 m²; Area Pane Right=2.41 m²; Clearvue Insulated LowE SHGC Value=0; Clearvue Insulated LowE U Value=7.9; Clearvue Insulated SHGC Value=0; Clearvue Insulated U Value=7.9; Clearvue SHGC Value=0; Clearvue U Value=7.9; Custom Sash Width=900 mm  [stored 2.95276 ft]; Custom Windload=1500 mm; Custom Window Height=1790 mm; Custom Window Width=2390 mm; DG Thickness Calc=5 mm  [stored 0.0164042 ft]; Depth Mullion=90 mm  [stored 0.295276 ft]; Energy Advantage SHGC Value=0; Energy Advantage U Value=7.9; Height=1790 mm; Height Panel 3=590 mm; Height Panel 4=1730 mm; Intruderprufe Insulated LowE SHGC Value=0.889; Intruderprufe Insulated LowE U Value=5.02; Intruderprufe Insulated SHGC Value=0.977; Intruderprufe Insulated U Value=6.05; Intruderprufe LowE SHGC Value=1.01; Intruderprufe LowE U Value=7.39; Intruderprufe SHGC Value=1.149; Intruderprufe U Value=10.29; Length Mullion=1790 mm; Length Transom=886 mm  [stored 2.90682 ft]; Limit Sash Bottom Height Max=900 mm  [stored 2.95276 ft]; Limit Sash Bottom Height Max Based On Top Sash=944 mm; Limit Sash Bottom Height Max Calc=900 mm  [stored 2.95276 ft]; Limit Window Width Max=2476 mm; Limit Window Width Min=1176 mm; Max Pane Area=2.41 m²; Mullion Depth Windload Based=90 mm  [stored 0.295276 ft]; Offset Mullion Left=916 mm  [stored 3.00525 ft]; Offset Panel 4 Left=946 mm; Width=2390 mm; Width Panel 1=886 mm  [stored 2.90682 ft]; Width Panel 2=886 mm  [stored 2.90682 ft]; Width Panel 3=886 mm  [stored 2.90682 ft]; Width Panel 4=1414 mm; Width Sash 1=870 mm  [stored 2.85433 ft]; Width Sash 2=870 mm  [stored 2.85433 ft]; Width Sash Opening=900 mm  [stored 2.95276 ft]; Windload Design=1500 mm
- 36-2418DT-2000Pa: Area Pane Left Bottom=0.51 m²; Area Pane Left Middle=0.4 m²; Area Pane Left Top=0.4 m²; Area Pane Right=2.41 m²; Clearvue Insulated LowE SHGC Value=0; Clearvue Insulated LowE U Value=7.9; Clearvue Insulated SHGC Value=0; Clearvue Insulated U Value=7.9; Clearvue SHGC Value=0; Clearvue U Value=7.9; Custom Sash Width=900 mm  [stored 2.95276 ft]; Custom Windload=2000 mm; Custom Window Height=1790 mm; Custom Window Width=2390 mm; DG Thickness Calc=5 mm  [stored 0.0164042 ft]; Depth Mullion=90 mm  [stored 0.295276 ft]; Energy Advantage SHGC Value=0; Energy Advantage U Value=7.9; Height=1790 mm; Height Panel 3=590 mm; Height Panel 4=1730 mm; Intruderprufe Insulated LowE SHGC Value=0.889; Intruderprufe Insulated LowE U Value=5.02; Intruderprufe Insulated SHGC Value=0.977; Intruderprufe Insulated U Value=6.05; Intruderprufe LowE SHGC Value=1.01; Intruderprufe LowE U Value=7.39; Intruderprufe SHGC Value=1.149; Intruderprufe U Value=10.29; Length Mullion=1790 mm; Length Transom=886 mm  [stored 2.90682 ft]; Limit Sash Bottom Height Max=900 mm  [stored 2.95276 ft]; Limit Sash Bottom Height Max Based On Top Sash=944 mm; Limit Sash Bottom Height Max Calc=900 mm  [stored 2.95276 ft]; Limit Window Width Max=2476 mm; Limit Window Width Min=1176 mm; Max Pane Area=2.41 m²; Mullion Depth Windload Based=90 mm  [stored 0.295276 ft]; Offset Mullion Left=916 mm  [stored 3.00525 ft]; Offset Panel 4 Left=946 mm; Width=2390 mm; Width Panel 1=886 mm  [stored 2.90682 ft]; Width Panel 2=886 mm  [stored 2.90682 ft]; Width Panel 3=886 mm  [stored 2.90682 ft]; Width Panel 4=1414 mm; Width Sash 1=870 mm  [stored 2.85433 ft]; Width Sash 2=870 mm  [stored 2.85433 ft]; Width Sash Opening=900 mm  [stored 2.95276 ft]; Windload Design=2000 mm

note: [stored X ft] marks values corroborated as IEEE doubles in the binary element streams (Revit-internal decimal feet)

## geometry (parser evidence)
native form markers: Blend x4, Extrusion x1, Sweep x29
no freeform markers — native parametric forms only
